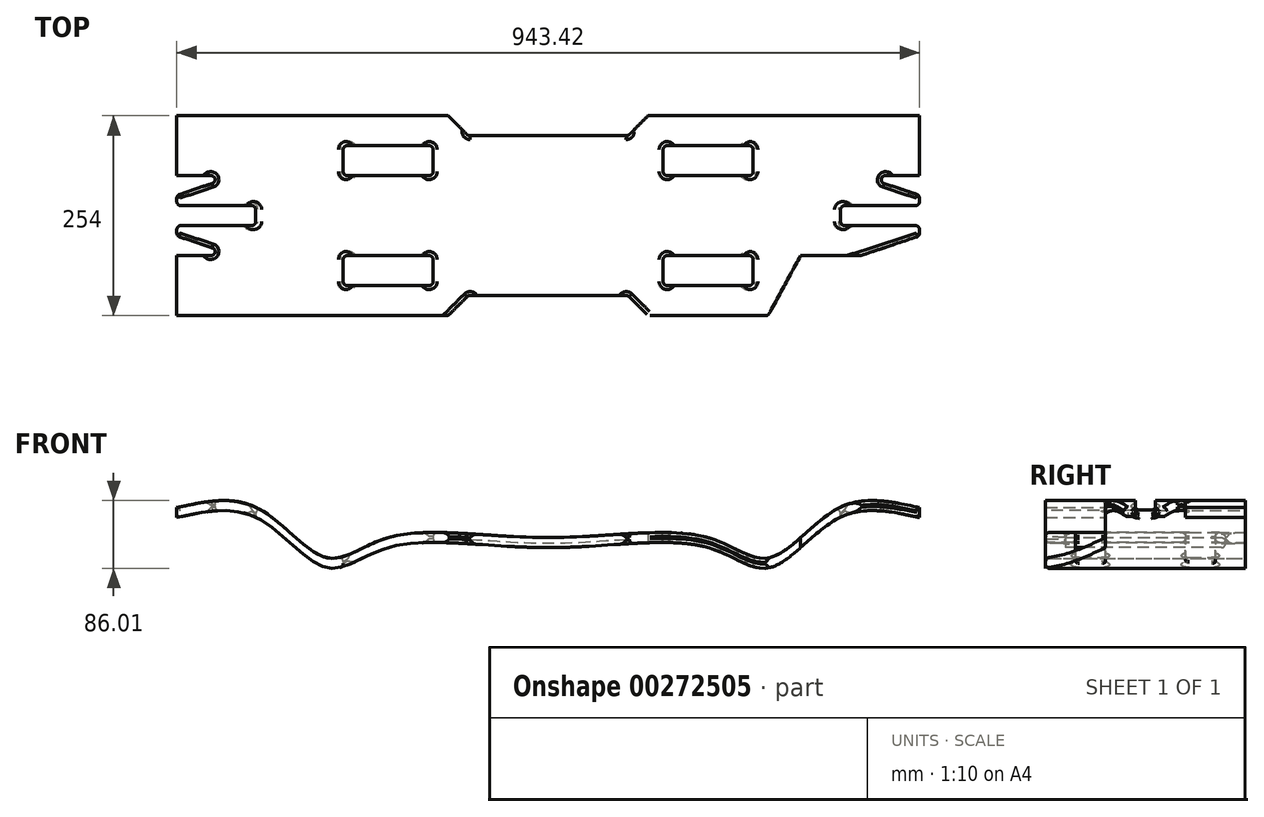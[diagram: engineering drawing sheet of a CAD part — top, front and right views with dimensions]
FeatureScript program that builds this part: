
annotation { "Feature Type Name" : "Feature", "Feature Type Description" : "" }
export const myFeature = defineFeature(function(context is Context, id is Id, definition is map)
    precondition{}
    {
        {
            var Q0;
            Q0=qCreatedBy(makeId("Front.planeOp"),FACE);
            var sketch = newSketch(context, id + "F0", { "sketchPlane" : qUnion([Q0])});
            skPoint(sketch, "E0.middle", {"position": v(0, 0) * mm});
            skLineSegment(sketch, "E1.right", {"start": v(-471.71, 57.15) * mm, "end": v(-471.71, 69.85) * mm});
            skLineSegment(sketch, "E2", {"start": v(-471.71, 69.85) * mm, "end": v(-471.71, 57.15) * mm});
            skLineSegment(sketch, "E3", {"start": v(471.71, 57.15) * mm, "end": v(471.71, 69.85) * mm});
            skPoint(sketch, "E4.endSnap0", {"position": v(0, 6.35) * mm});
            skPoint(sketch, "E4.start.orphan", {"position": v(0, -6.35) * mm});
            skPoint(sketch, "E5.trimOffspring.end.orphan", {"position": v(0, 19.05) * mm});
            skPoint(sketch, "E6.start.orphan", {"position": v(228.6, 19.05) * mm});
            skPoint(sketch, "E7.end.orphan", {"position": v(-228.6, 19.05) * mm});
            skFitSpline(sketch, "E8", {"points": [v(-471.71, 57.15) * mm, v(-370.11, 57.15) * mm, v(-281.21, -6.35) * mm, v(-203.2, 19.05) * mm, v(0, 19.05) * mm, v(203.2, 19.05) * mm, v(281.21, -6.35) * mm, v(370.11, 57.15) * mm, v(471.71, 57.15) * mm], "startDerivative": vector(913.94, 203.4) * mm, "endDerivative": vector(913.94, -203.4) * mm});
            skFitSpline(sketch, "E9", {"points": [v(471.71, 69.85) * mm, v(370.11, 69.85) * mm, v(281.21, 6.35) * mm, v(203.2, 31.75) * mm, v(0, 31.75) * mm, v(-203.2, 31.75) * mm, v(-281.21, 6.35) * mm, v(-370.11, 69.85) * mm, v(-471.71, 69.85) * mm], "startDerivative": vector(-913.94, 203.4) * mm, "endDerivative": vector(-913.94, -203.4) * mm});
            skPoint(sketch, "E0.right.end.orphan", {"position": v(-319.31, -6.35) * mm});
            skPoint(sketch, "E0.right.start.orphan", {"position": v(-319.31, 6.35) * mm});
            skSolve(sketch);
        }
        {
            var Q0;
            Q0=qSketchRegion(id+"F0",true);
            extrude(context, id + "F1", {"entities" : qUnion([Q0]), "depth" : 127 * mm, "offsetDistance" : 25.4 * mm, "hasSecondDirection" : true, "secondDirectionOppositeDirection" : true, "secondDirectionDepth" : 127 * mm});
        }
        {
            var Q0;
            Q0=qCreatedBy(makeId("Top.planeOp"),FACE);
            var sketch = newSketch(context, id + "F2", { "sketchPlane" : qUnion([Q0])});
            skLineSegment(sketch, "E10.bottom", {"start": v(473.08, -127) * mm, "end": v(279.4, -127) * mm});
            skLineSegment(sketch, "E10.top", {"start": v(473.08, 127) * mm, "end": v(-473.08, 127) * mm});
            skLineSegment(sketch, "E10.left", {"start": v(473.08, -50.8) * mm, "end": v(473.08, 127) * mm});
            skLineSegment(sketch, "E10.right", {"start": v(-473.08, -127) * mm, "end": v(-473.08, 127) * mm});
            skPoint(sketch, "E10.middle", {"position": v(0, 0) * mm});
            skLineSegment(sketch, "E11", {"start": v(-473.08, -127) * mm, "end": v(-473.08, -50.8) * mm});
            skLineSegment(sketch, "E12", {"start": v(473.08, -127) * mm, "end": v(473.08, -50.8) * mm});
            skLineSegment(sketch, "E13.bottom", {"start": v(-473.08, -50.8) * mm, "end": v(-320.68, -50.8) * mm});
            skLineSegment(sketch, "E13.top", {"start": v(-473.08, 50.8) * mm, "end": v(-320.68, 50.8) * mm});
            skLineSegment(sketch, "E13.left", {"start": v(-473.08, -50.8) * mm, "end": v(-473.08, 50.8) * mm});
            skLineSegment(sketch, "E13.right", {"start": v(-320.68, -50.8) * mm, "end": v(-320.68, 50.8) * mm});
            skLineSegment(sketch, "E14.bottom", {"start": v(473.08, -50.8) * mm, "end": v(320.67, -50.8) * mm});
            skLineSegment(sketch, "E14.top", {"start": v(473.07, 50.8) * mm, "end": v(320.67, 50.8) * mm});
            skLineSegment(sketch, "E14.left", {"start": v(473.08, -50.8) * mm, "end": v(473.08, 50.8) * mm});
            skLineSegment(sketch, "E14.right", {"start": v(320.67, -50.8) * mm, "end": v(320.67, 50.8) * mm});
            skLineSegment(sketch, "E15.bottom", {"start": v(127, -127) * mm, "end": v(-279.4, -127) * mm});
            skLineSegment(sketch, "E15.top", {"start": v(279.4, 127) * mm, "end": v(-279.4, 127) * mm});
            skLineSegment(sketch, "E15.left", {"start": v(279.4, -127) * mm, "end": v(279.4, 127) * mm});
            skLineSegment(sketch, "E15.right", {"start": v(-279.4, -127) * mm, "end": v(-279.4, 127) * mm});
            skLineSegment(sketch, "E16", {"start": v(-473.08, 0) * mm, "end": v(-422.28, 0) * mm});
            skLineSegment(sketch, "E17", {"start": v(473.08, 0) * mm, "end": v(422.28, 0) * mm});
            skLineSegment(sketch, "E18.bottom", {"start": v(-473.08, -12.7) * mm, "end": v(-371.48, -12.7) * mm});
            skLineSegment(sketch, "E18.top", {"start": v(-473.08, 12.7) * mm, "end": v(-371.48, 12.7) * mm});
            skLineSegment(sketch, "E18.left", {"start": v(-473.08, -12.7) * mm, "end": v(-473.08, 12.7) * mm});
            skLineSegment(sketch, "E18.right", {"start": v(-371.48, -12.7) * mm, "end": v(-371.48, 12.7) * mm});
            skPoint(sketch, "E18.middle", {"position": v(-422.28, 0) * mm});
            skLineSegment(sketch, "E19.bottom", {"start": v(473.08, -12.7) * mm, "end": v(371.48, -12.7) * mm});
            skLineSegment(sketch, "E19.top", {"start": v(473.08, 12.7) * mm, "end": v(371.48, 12.7) * mm});
            skLineSegment(sketch, "E19.left", {"start": v(473.08, -12.7) * mm, "end": v(473.08, 12.7) * mm});
            skLineSegment(sketch, "E19.right", {"start": v(371.48, -12.7) * mm, "end": v(371.48, 12.7) * mm});
            skPoint(sketch, "E19.middle", {"position": v(422.28, 0) * mm});
            skLineSegment(sketch, "E20", {"start": v(-473.08, 0) * mm, "end": v(-473.08, -50.8) * mm});
            skLineSegment(sketch, "E21", {"start": v(-473.08, 0) * mm, "end": v(-473.08, 50.8) * mm});
            skLineSegment(sketch, "E22", {"start": v(473.08, 50.8) * mm, "end": v(473.08, 0) * mm});
            skLineSegment(sketch, "E23", {"start": v(473.08, 0) * mm, "end": v(473.08, -50.8) * mm});
            skLineSegment(sketch, "E24", {"start": v(-473.08, -12.7) * mm, "end": v(-473.08, -25.4) * mm});
            skLineSegment(sketch, "E25", {"start": v(-473.08, -25.4) * mm, "end": v(-396.88, -50.8) * mm});
            skLineSegment(sketch, "E26", {"start": v(-396.88, -50.8) * mm, "end": v(-320.68, -50.8) * mm});
            skLineSegment(sketch, "E27", {"start": v(-320.68, -50.8) * mm, "end": v(-279.4, -127) * mm});
            skLineSegment(sketch, "E28", {"start": v(279.4, -127) * mm, "end": v(320.68, -50.8) * mm});
            skLineSegment(sketch, "E29", {"start": v(396.88, -50.8) * mm, "end": v(473.08, -25.4) * mm});
            skLineSegment(sketch, "E30", {"start": v(473.08, -25.4) * mm, "end": v(473.08, -12.7) * mm});
            skLineSegment(sketch, "E31", {"start": v(473.08, 12.7) * mm, "end": v(473.08, 25.4) * mm});
            skLineSegment(sketch, "E32", {"start": v(473.08, 25.4) * mm, "end": v(396.88, 50.8) * mm});
            skLineSegment(sketch, "E33", {"start": v(396.88, 50.8) * mm, "end": v(320.67, 50.8) * mm});
            skLineSegment(sketch, "E34", {"start": v(320.67, 50.8) * mm, "end": v(279.4, 127) * mm});
            skLineSegment(sketch, "E35", {"start": v(-279.4, 127) * mm, "end": v(-320.67, 50.8) * mm});
            skLineSegment(sketch, "E36", {"start": v(-396.88, 50.8) * mm, "end": v(-473.08, 25.4) * mm});
            skLineSegment(sketch, "E37", {"start": v(-473.08, 25.4) * mm, "end": v(-473.08, 12.7) * mm});
            skLineSegment(sketch, "E38", {"start": v(0, 127) * mm, "end": v(0, -127) * mm});
            skLineSegment(sketch, "E39.bottom", {"start": v(101.6, -101.6) * mm, "end": v(-101.6, -101.6) * mm});
            skLineSegment(sketch, "E39.top", {"start": v(101.6, 101.6) * mm, "end": v(-101.6, 101.6) * mm});
            skLineSegment(sketch, "E39.left", {"start": v(101.6, -101.6) * mm, "end": v(101.6, 101.6) * mm});
            skLineSegment(sketch, "E39.right", {"start": v(-101.6, -101.6) * mm, "end": v(-101.6, 101.6) * mm});
            skLineSegment(sketch, "E40", {"start": v(-279.4, -127) * mm, "end": v(-127, -127) * mm});
            skLineSegment(sketch, "E41", {"start": v(-279.4, 127) * mm, "end": v(-127, 127) * mm});
            skLineSegment(sketch, "E42", {"start": v(279.4, 127) * mm, "end": v(127, 127) * mm});
            skLineSegment(sketch, "E43", {"start": v(279.4, -127) * mm, "end": v(127, -127) * mm});
            skLineSegment(sketch, "E44.trimOffspring", {"start": v(127, -127) * mm, "end": v(-473.08, -127) * mm});
            skLineSegment(sketch, "E45", {"start": v(-127, 127) * mm, "end": v(-101.6, 101.6) * mm});
            skLineSegment(sketch, "E46", {"start": v(127, 127) * mm, "end": v(101.6, 101.6) * mm});
            skLineSegment(sketch, "E47", {"start": v(101.6, -101.6) * mm, "end": v(127, -127) * mm});
            skLineSegment(sketch, "E48", {"start": v(-101.6, -101.6) * mm, "end": v(-127, -127) * mm});
            skLineSegment(sketch, "E49.bottom", {"start": v(-260.35, 50.8) * mm, "end": v(-146.05, 50.8) * mm});
            skLineSegment(sketch, "E49.top", {"start": v(-260.35, 88.9) * mm, "end": v(-146.05, 88.9) * mm});
            skLineSegment(sketch, "E49.left", {"start": v(-260.35, 50.8) * mm, "end": v(-260.35, 88.9) * mm});
            skLineSegment(sketch, "E49.right", {"start": v(-146.05, 50.8) * mm, "end": v(-146.05, 88.9) * mm});
            skLineSegment(sketch, "E50.bottom", {"start": v(-260.35, -88.9) * mm, "end": v(-146.05, -88.9) * mm});
            skLineSegment(sketch, "E50.top", {"start": v(-260.35, -50.8) * mm, "end": v(-146.05, -50.8) * mm});
            skLineSegment(sketch, "E50.left", {"start": v(-260.35, -88.9) * mm, "end": v(-260.35, -50.8) * mm});
            skLineSegment(sketch, "E50.right", {"start": v(-146.05, -88.9) * mm, "end": v(-146.05, -50.8) * mm});
            skLineSegment(sketch, "E51.bottom", {"start": v(146.05, -88.9) * mm, "end": v(260.35, -88.9) * mm});
            skLineSegment(sketch, "E51.top", {"start": v(146.05, -50.8) * mm, "end": v(260.35, -50.8) * mm});
            skLineSegment(sketch, "E51.left", {"start": v(146.05, -88.9) * mm, "end": v(146.05, -50.8) * mm});
            skLineSegment(sketch, "E51.right", {"start": v(260.35, -88.9) * mm, "end": v(260.35, -50.8) * mm});
            skLineSegment(sketch, "E52.bottom", {"start": v(146.05, 50.8) * mm, "end": v(260.35, 50.8) * mm});
            skLineSegment(sketch, "E52.top", {"start": v(146.05, 88.9) * mm, "end": v(260.35, 88.9) * mm});
            skLineSegment(sketch, "E52.left", {"start": v(146.05, 50.8) * mm, "end": v(146.05, 88.9) * mm});
            skLineSegment(sketch, "E52.right", {"start": v(260.35, 50.8) * mm, "end": v(260.35, 88.9) * mm});
            skLineSegment(sketch, "E53", {"start": v(-203.2, -88.9) * mm, "end": v(-203.2, -127) * mm});
            skLineSegment(sketch, "E54", {"start": v(-203.2, 88.9) * mm, "end": v(-203.2, 127) * mm});
            skLineSegment(sketch, "E55", {"start": v(203.2, 127) * mm, "end": v(203.2, 88.9) * mm});
            skLineSegment(sketch, "E56", {"start": v(203.2, -88.9) * mm, "end": v(203.2, -127) * mm});
            skSolve(sketch);
        }
        {
            var Q0;
            {var subQ5=sQuery(id+"F2.wireOp",EDGE,"E48");Q0=makeQuery(id+"F2.imprint","IMPRINT",FACE,{"disambiguationData":[TD([[makeQuery(id+"F2.imprint","IMPRINT",EDGE,{"derivedFrom":subQ5}),1.0]])]});}
            var Q1;
            {var subQ5=sQuery(id+"F2.wireOp",EDGE,"E47");Q1=makeQuery(id+"F2.imprint","IMPRINT",FACE,{"disambiguationData":[TD([[makeQuery(id+"F2.imprint","IMPRINT",EDGE,{"derivedFrom":subQ5}),-1.0]])]});}
            var Q2;
            Q2=makeQuery(id+"F2.imprint","IMPRINT",FACE,{"disambiguationData":[TD([[makeQuery(id+"F2.imprint","IMPRINT",EDGE,{"derivedFrom":sQuery(id+"F2.wireOp",EDGE,"E50.top")}),-1.0]])]});
            var Q3;
            Q3=makeQuery(id+"F2.imprint","IMPRINT",FACE,{"disambiguationData":[TD([[makeQuery(id+"F2.imprint","IMPRINT",EDGE,{"derivedFrom":sQuery(id+"F2.wireOp",EDGE,"E49.bottom")}),1.0]])]});
            var Q4;
            {var subQ0=sQuery(id+"F2.wireOp",EDGE,"E45");Q4=makeQuery(id+"F2.imprint","IMPRINT",FACE,{"disambiguationData":[TD([[makeQuery(id+"F2.imprint","IMPRINT",EDGE,{"derivedFrom":subQ0}),1.0]])]});}
            var Q5;
            {var subQ0=sQuery(id+"F2.wireOp",EDGE,"E46");Q5=makeQuery(id+"F2.imprint","IMPRINT",FACE,{"disambiguationData":[TD([[makeQuery(id+"F2.imprint","IMPRINT",EDGE,{"derivedFrom":subQ0}),-1.0]])]});}
            var Q6;
            Q6=makeQuery(id+"F2.imprint","IMPRINT",FACE,{"disambiguationData":[TD([[makeQuery(id+"F2.imprint","IMPRINT",EDGE,{"derivedFrom":sQuery(id+"F2.wireOp",EDGE,"E52.bottom")}),1.0]])]});
            var Q7;
            Q7=makeQuery(id+"F2.imprint","IMPRINT",FACE,{"disambiguationData":[TD([[makeQuery(id+"F2.imprint","IMPRINT",EDGE,{"derivedFrom":sQuery(id+"F2.wireOp",EDGE,"E51.top")}),-1.0]])]});
            var Q8;
            Q8=makeQuery(id+"F2.imprint","IMPRINT",FACE,{"disambiguationData":[TD([[makeQuery(id+"F2.imprint","IMPRINT",EDGE,{"derivedFrom":sQuery(id+"F2.wireOp",EDGE,"E10.bottom")}),-1.0]])]});
            var Q9;
            {var subQ4=sQuery(id+"F2.wireOp",EDGE,"E19.bottom");Q9=makeQuery(id+"F2.imprint","IMPRINT",FACE,{"disambiguationData":[TD([[makeQuery(id+"F2.imprint","IMPRINT",EDGE,{"derivedFrom":subQ4}),-1.0]])]});}
            var Q10;
            {var subQ3=sQuery(id+"F2.wireOp",EDGE,"E29");Q10=makeQuery(id+"F2.imprint","IMPRINT",FACE,{"disambiguationData":[TD([[makeQuery(id+"F2.imprint","IMPRINT",EDGE,{"derivedFrom":subQ3}),-1.0]])]});}
            var Q11;
            {var subQ1=sQuery(id+"F2.wireOp",EDGE,"E10.right");Q11=makeQuery(id+"F2.imprint","IMPRINT",FACE,{"disambiguationData":[TD([[makeQuery(id+"F2.imprint","IMPRINT",EDGE,{"derivedFrom":subQ1}),-1.0]])]});}
            var Q12;
            {var subQ3=sQuery(id+"F2.wireOp",EDGE,"E36");Q12=makeQuery(id+"F2.imprint","IMPRINT",FACE,{"disambiguationData":[TD([[makeQuery(id+"F2.imprint","IMPRINT",EDGE,{"derivedFrom":subQ3}),-1.0]])]});}
            var Q13;
            {var subQ3=sQuery(id+"F2.wireOp",EDGE,"E18.bottom");Q13=makeQuery(id+"F2.imprint","IMPRINT",FACE,{"disambiguationData":[TD([[makeQuery(id+"F2.imprint","IMPRINT",EDGE,{"derivedFrom":subQ3}),1.0]])]});}
            var Q14;
            {var subQ0=sQuery(id+"F2.wireOp",EDGE,"E13.bottom");Q14=makeQuery(id+"F2.imprint","IMPRINT",FACE,{"disambiguationData":[TD([[makeQuery(id+"F2.imprint","IMPRINT",EDGE,{"derivedFrom":subQ0}),1.0]])]});}
            var Q15;
            {var subQ1=sQuery(id+"F2.wireOp",EDGE,"E11");Q15=makeQuery(id+"F2.imprint","IMPRINT",FACE,{"disambiguationData":[TD([[makeQuery(id+"F2.imprint","IMPRINT",EDGE,{"derivedFrom":subQ1}),-1.0]])]});}
            var Q16;
            {var subQ0=sQuery(id+"F2.wireOp",EDGE,"E10.left");Q16=makeQuery(id+"F2.imprint","IMPRINT",FACE,{"disambiguationData":[TD([[makeQuery(id+"F2.imprint","IMPRINT",EDGE,{"derivedFrom":subQ0}),1.0]])]});}
            var Q17;
            {var subQ0=sQuery(id+"F2.wireOp",EDGE,"E14.top");Q17=makeQuery(id+"F2.imprint","IMPRINT",FACE,{"disambiguationData":[TD([[makeQuery(id+"F2.imprint","IMPRINT",EDGE,{"derivedFrom":subQ0}),1.0]])]});}
            extrude(context, id + "F3", {"entities" : qUnion([Q0, Q1, Q2, Q3, Q4, Q5, Q6, Q7, Q8, Q9, Q10, Q11, Q12, Q13, Q14, Q15, Q16, Q17]), "operationType" : NewBodyOperationType.REMOVE, "depth" : 127 * mm, "offsetDistance" : 25.4 * mm, "hasSecondDirection" : true, "secondDirectionOppositeDirection" : true, "secondDirectionDepth" : 25.4 * mm});
        }
        {
            var Q0;
            Q0=makeQuery(id+"F3.boolean.opBoolean","COPY",FACE,{"derivedFrom":makeQuery(id+"F3.opExtrude","SWEPT_FACE",FACE,{"disambiguationData":[OSD([sQuery(id+"F2.wireOp",EDGE,"E49.left")])]})});
            var Q1;
            Q1=makeQuery(id+"F3.boolean.opBoolean","COPY",FACE,{"derivedFrom":makeQuery(id+"F3.opExtrude","SWEPT_FACE",FACE,{"disambiguationData":[OSD([sQuery(id+"F2.wireOp",EDGE,"E49.right")])]})});
            var Q2;
            Q2=makeQuery(id+"F3.boolean.opBoolean","COPY",FACE,{"derivedFrom":makeQuery(id+"F3.opExtrude","SWEPT_FACE",FACE,{"disambiguationData":[OSD([sQuery(id+"F2.wireOp",EDGE,"E50.left")])]})});
            var Q3;
            Q3=makeQuery(id+"F3.boolean.opBoolean","COPY",FACE,{"derivedFrom":makeQuery(id+"F3.opExtrude","SWEPT_FACE",FACE,{"disambiguationData":[OSD([sQuery(id+"F2.wireOp",EDGE,"E50.right")])]})});
            fillet(context, id + "F4", {"entities" : qUnion([Q0, Q1, Q2, Q3]), "radius" : 5.08 * mm, "tangentPropagation" : true, "allowEdgeOverflow" : false});
        }
        {
            var Q0;
            Q0=makeQuery(id+"F3.boolean.opBoolean","COPY",FACE,{"derivedFrom":makeQuery(id+"F3.opExtrude","SWEPT_FACE",FACE,{"disambiguationData":[OSD([sQuery(id+"F2.wireOp",EDGE,"E52.right")])]})});
            var Q1;
            Q1=makeQuery(id+"F3.boolean.opBoolean","COPY",FACE,{"derivedFrom":makeQuery(id+"F3.opExtrude","SWEPT_FACE",FACE,{"disambiguationData":[OSD([sQuery(id+"F2.wireOp",EDGE,"E52.left")])]})});
            var Q2;
            Q2=makeQuery(id+"F3.boolean.opBoolean","COPY",FACE,{"derivedFrom":makeQuery(id+"F3.opExtrude","SWEPT_FACE",FACE,{"disambiguationData":[OSD([sQuery(id+"F2.wireOp",EDGE,"E51.left")])]})});
            var Q3;
            Q3=makeQuery(id+"F3.boolean.opBoolean","COPY",FACE,{"derivedFrom":makeQuery(id+"F3.opExtrude","SWEPT_FACE",FACE,{"disambiguationData":[OSD([sQuery(id+"F2.wireOp",EDGE,"E51.right")])]})});
            fillet(context, id + "F5", {"entities" : qUnion([Q0, Q1, Q2, Q3]), "radius" : 5.08 * mm, "tangentPropagation" : true, "allowEdgeOverflow" : false});
        }
        {
            var Q0;
            Q0=makeQuery(id+"F3.boolean.opBoolean","COPY",FACE,{"derivedFrom":makeQuery(id+"F3.opExtrude","SWEPT_FACE",FACE,{"disambiguationData":[OSD([sQuery(id+"F2.wireOp",EDGE,"E19.right")])]})});
            var Q1;
            Q1=makeQuery(id+"F3.boolean.opBoolean","SPLIT",FACE,{"disambiguationData":[TD([makeQuery(id+"F3.opExtrude","SWEPT_FACE",FACE,{"disambiguationData":[OSD([sQuery(id+"F2.wireOp",EDGE,"E19.bottom")])]})])],"derivedFrom":makeQuery(id+"F1.opExtrude","SWEPT_FACE",FACE,{"disambiguationData":[OSD([sQuery(id+"F0.wireOp",EDGE,"E3")])]})});
            var Q2;
            Q2=makeQuery(id+"F3.boolean.opBoolean","SPLIT",FACE,{"disambiguationData":[TD([makeQuery(id+"F3.opExtrude","SWEPT_FACE",FACE,{"disambiguationData":[OSD([sQuery(id+"F2.wireOp",EDGE,"E19.top")])]})])],"derivedFrom":makeQuery(id+"F1.opExtrude","SWEPT_FACE",FACE,{"disambiguationData":[OSD([sQuery(id+"F0.wireOp",EDGE,"E3")])]})});
            var Q3;
            Q3=makeQuery(id+"F3.boolean.opBoolean","COPY",FACE,{"derivedFrom":makeQuery(id+"F3.opExtrude","SWEPT_FACE",FACE,{"disambiguationData":[OSD([sQuery(id+"F2.wireOp",EDGE,"E32")])]})});
            var Q4;
            Q4=makeQuery(id+"F3.boolean.opBoolean","COPY",FACE,{"derivedFrom":makeQuery(id+"F3.opExtrude","SWEPT_FACE",FACE,{"disambiguationData":[OSD([sQuery(id+"F2.wireOp",EDGE,"E29")])]})});
            fillet(context, id + "F6", {"entities" : qUnion([Q0, Q1, Q2, Q3, Q4]), "radius" : 5.08 * mm, "tangentPropagation" : true, "allowEdgeOverflow" : false});
        }
        {
            var Q0;
            {var subQ0=sQuery(id+"F0.wireOp",EDGE,"E8");var subQ1=sQuery(id+"F0.wireOp",EDGE,"E9");Q0=makeQuery(id+"F3.boolean.opBoolean","SPLIT",FACE,{"disambiguationData":[TD([makeQuery(id+"F3.opExtrude","SWEPT_FACE",FACE,{"disambiguationData":[OSD([sQuery(id+"F2.wireOp",EDGE,"E28")])]})])],"derivedFrom":makeQuery(id+"F1.opExtrude","CAP_FACE",FACE,{"disambiguationData":[OSD([sQuery(id+"F0.wireOp",EDGE,"E3"),sQuery(id+"F0.wireOp",EDGE,"E1.right"),subQ0,subQ1])],"isStart":false})});}
            var Q1;
            Q1=makeQuery(id+"F3.boolean.opBoolean","COPY",FACE,{"derivedFrom":makeQuery(id+"F3.opExtrude","SWEPT_FACE",FACE,{"disambiguationData":[OSD([sQuery(id+"F2.wireOp",EDGE,"E47")])]})});
            var Q2;
            Q2=makeQuery(id+"F3.boolean.opBoolean","COPY",FACE,{"derivedFrom":makeQuery(id+"F3.opExtrude","SWEPT_FACE",FACE,{"disambiguationData":[OSD([sQuery(id+"F2.wireOp",EDGE,"E48")])]})});
            var Q3;
            {var subQ0=sQuery(id+"F0.wireOp",EDGE,"E8");var subQ1=sQuery(id+"F0.wireOp",EDGE,"E9");Q3=makeQuery(id+"F3.boolean.opBoolean","SPLIT",FACE,{"disambiguationData":[TD([makeQuery(id+"F3.opExtrude","SWEPT_FACE",FACE,{"disambiguationData":[OSD([sQuery(id+"F2.wireOp",EDGE,"E27")])]})])],"derivedFrom":makeQuery(id+"F1.opExtrude","CAP_FACE",FACE,{"disambiguationData":[OSD([sQuery(id+"F0.wireOp",EDGE,"E3"),sQuery(id+"F0.wireOp",EDGE,"E1.right"),subQ0,subQ1])],"isStart":false})});}
            fillet(context, id + "F7", {"entities" : qUnion([Q0, Q1, Q2, Q3]), "radius" : 5.08 * mm, "tangentPropagation" : true, "allowEdgeOverflow" : false});
        }
        {
            var Q0;
            Q0=makeQuery(id+"F3.boolean.opBoolean","COPY",FACE,{"derivedFrom":makeQuery(id+"F3.opExtrude","SWEPT_FACE",FACE,{"disambiguationData":[OSD([sQuery(id+"F2.wireOp",EDGE,"E18.right")])]})});
            var Q1;
            Q1=makeQuery(id+"F3.boolean.opBoolean","SPLIT",FACE,{"disambiguationData":[TD([makeQuery(id+"F3.opExtrude","SWEPT_FACE",FACE,{"disambiguationData":[OSD([sQuery(id+"F2.wireOp",EDGE,"E18.bottom")])]})])],"derivedFrom":makeQuery(id+"F1.opExtrude","SWEPT_FACE",FACE,{"disambiguationData":[OSD([sQuery(id+"F0.wireOp",EDGE,"E1.right")])]})});
            var Q2;
            Q2=makeQuery(id+"F3.boolean.opBoolean","SPLIT",FACE,{"disambiguationData":[TD([makeQuery(id+"F3.opExtrude","SWEPT_FACE",FACE,{"disambiguationData":[OSD([sQuery(id+"F2.wireOp",EDGE,"E18.top")])]})])],"derivedFrom":makeQuery(id+"F1.opExtrude","SWEPT_FACE",FACE,{"disambiguationData":[OSD([sQuery(id+"F0.wireOp",EDGE,"E1.right")])]})});
            var Q3;
            Q3=makeQuery(id+"F3.boolean.opBoolean","COPY",FACE,{"derivedFrom":makeQuery(id+"F3.opExtrude","SWEPT_FACE",FACE,{"disambiguationData":[OSD([sQuery(id+"F2.wireOp",EDGE,"E25")])]})});
            var Q4;
            Q4=makeQuery(id+"F3.boolean.opBoolean","COPY",FACE,{"derivedFrom":makeQuery(id+"F3.opExtrude","SWEPT_FACE",FACE,{"disambiguationData":[OSD([sQuery(id+"F2.wireOp",EDGE,"E36")])]})});
            fillet(context, id + "F8", {"entities" : qUnion([Q0, Q1, Q2, Q3, Q4]), "radius" : 5.08 * mm, "tangentPropagation" : true, "allowEdgeOverflow" : false});
        }
        {
            var Q0;
            Q0=makeQuery(id+"F3.boolean.opBoolean","COPY",FACE,{"derivedFrom":makeQuery(id+"F3.opExtrude","SWEPT_FACE",FACE,{"disambiguationData":[OSD([sQuery(id+"F2.wireOp",EDGE,"E39.top")])]})});
            var Q1;
            {var subQ0=sQuery(id+"F0.wireOp",EDGE,"E8");var subQ1=sQuery(id+"F0.wireOp",EDGE,"E9");Q1=makeQuery(id+"F3.boolean.opBoolean","SPLIT",FACE,{"disambiguationData":[TD([makeQuery(id+"F3.opExtrude","SWEPT_FACE",FACE,{"disambiguationData":[OSD([sQuery(id+"F2.wireOp",EDGE,"E35")])]})])],"derivedFrom":makeQuery(id+"F1.opExtrude","CAP_FACE",FACE,{"disambiguationData":[OSD([sQuery(id+"F0.wireOp",EDGE,"E3"),sQuery(id+"F0.wireOp",EDGE,"E1.right"),subQ0,subQ1])],"isStart":true})});}
            var Q2;
            {var subQ0=sQuery(id+"F0.wireOp",EDGE,"E8");var subQ1=sQuery(id+"F0.wireOp",EDGE,"E9");Q2=makeQuery(id+"F3.boolean.opBoolean","SPLIT",FACE,{"disambiguationData":[TD([makeQuery(id+"F3.opExtrude","SWEPT_FACE",FACE,{"disambiguationData":[OSD([sQuery(id+"F2.wireOp",EDGE,"E34")])]})])],"derivedFrom":makeQuery(id+"F1.opExtrude","CAP_FACE",FACE,{"disambiguationData":[OSD([sQuery(id+"F0.wireOp",EDGE,"E3"),sQuery(id+"F0.wireOp",EDGE,"E1.right"),subQ0,subQ1])],"isStart":true})});}
            fillet(context, id + "F9", {"entities" : qUnion([Q0, Q1, Q2]), "radius" : 5.08 * mm, "tangentPropagation" : true, "allowEdgeOverflow" : false});
        }
    });
